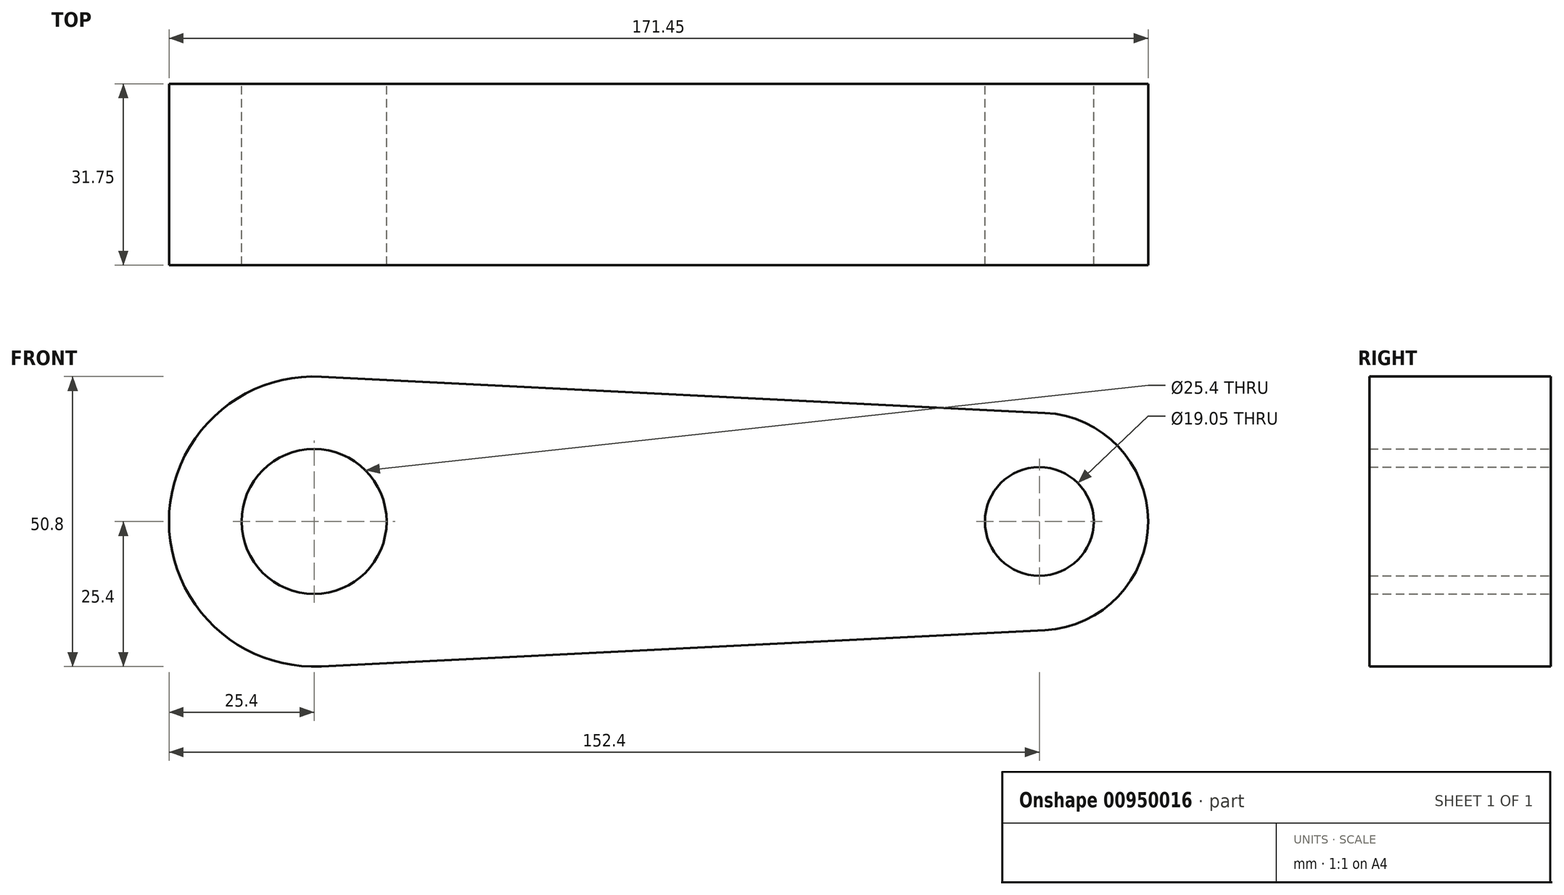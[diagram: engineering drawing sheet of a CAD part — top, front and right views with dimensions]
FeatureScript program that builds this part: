
annotation { "Feature Type Name" : "Feature", "Feature Type Description" : "" }
export const myFeature = defineFeature(function(context is Context, id is Id, definition is map)
    precondition{}
    {
        {
            var Q0;
            Q0=qCreatedBy(makeId("Front.planeOp"),FACE);
            var sketch = newSketch(context, id + "F0", { "sketchPlane" : qUnion([Q0])});
            skCircle(sketch, "E0", {"center": v(0, 0) * mm, "radius": 25.4 * mm});
            skCircle(sketch, "E1", {"center": v(127, 0) * mm, "radius": 19.05 * mm});
            skLineSegment(sketch, "E2", {"start": v(1.27, 25.37) * mm, "end": v(127.95, 19.03) * mm});
            skLineSegment(sketch, "E3", {"start": v(1.27, -25.37) * mm, "end": v(127.95, -19.03) * mm});
            skCircle(sketch, "E4", {"center": v(0, 0) * mm, "radius": 12.7 * mm});
            skCircle(sketch, "E5", {"center": v(127, 0) * mm, "radius": 9.53 * mm});
            skSolve(sketch);
        }
        {
            var Q0;
            Q0 = qSketchRegion(id + "F0", true);
            extrude(context, id + "F1", {"entities" : qUnion([Q0]), "depth" : 31.75 * mm, "offsetDistance" : 25.4 * mm});
        }
    });
